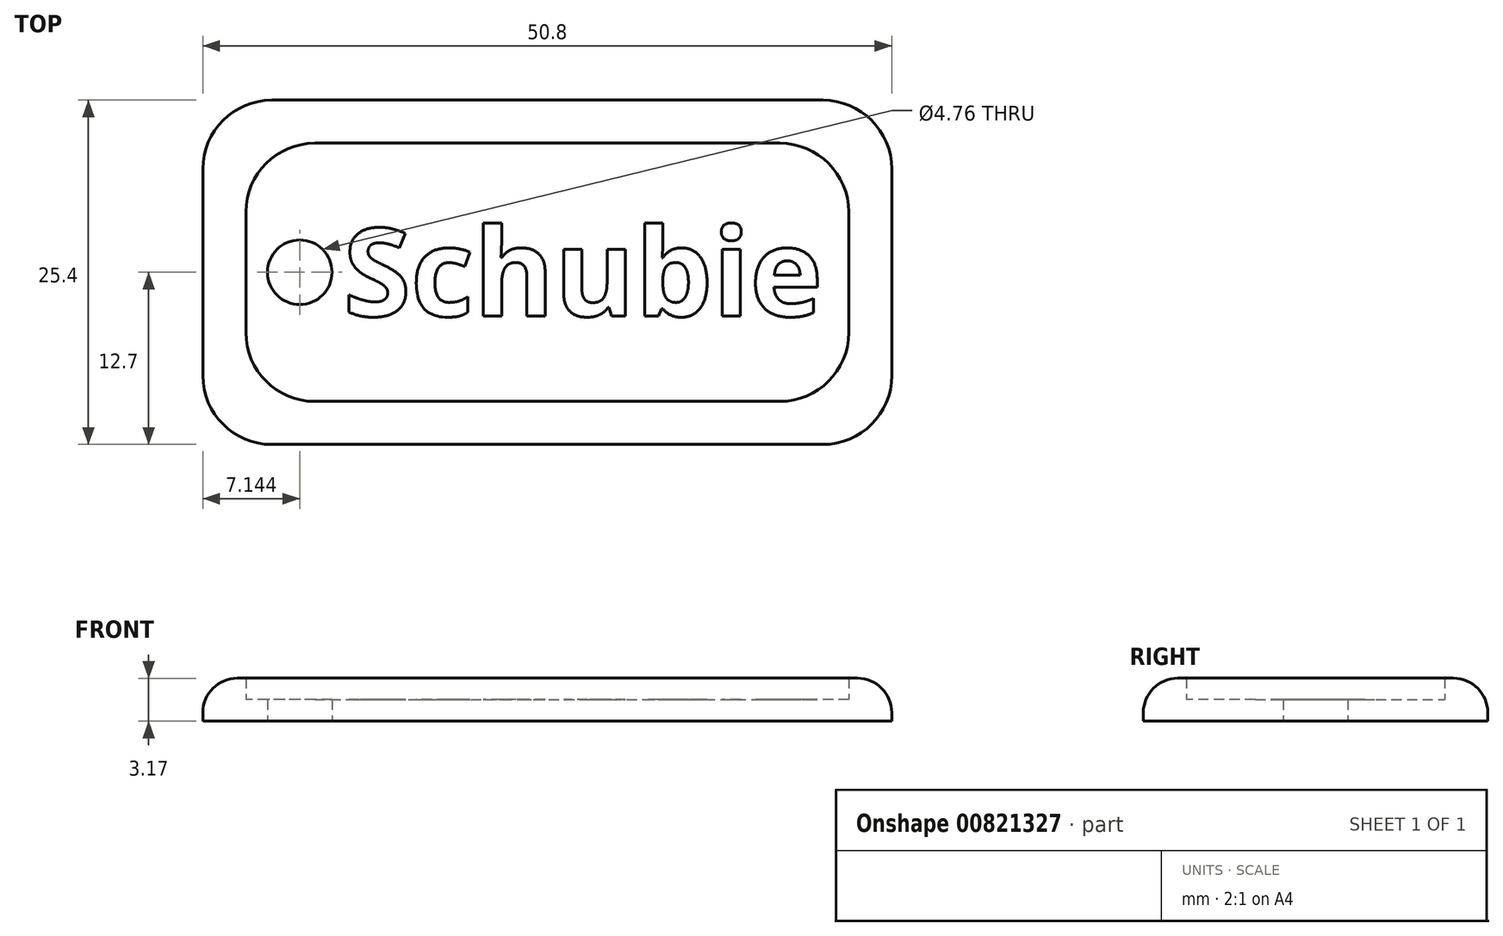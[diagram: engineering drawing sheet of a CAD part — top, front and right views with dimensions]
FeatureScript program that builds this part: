
annotation { "Feature Type Name" : "Feature", "Feature Type Description" : "" }
export const myFeature = defineFeature(function(context is Context, id is Id, definition is map)
    precondition{}
    {
        {
            var Q0;
            Q0=qCreatedBy(makeId("Top.planeOp"),FACE);
            var sketch = newSketch(context, id + "F0", { "sketchPlane" : qUnion([Q0])});
            skLineSegment(sketch, "E0.bottom", {"start": v(0, 0) * mm, "end": v(50.8, 0) * mm});
            skLineSegment(sketch, "E0.top", {"start": v(0, 25.4) * mm, "end": v(50.8, 25.4) * mm});
            skLineSegment(sketch, "E0.left", {"start": v(0, 0) * mm, "end": v(0, 25.4) * mm});
            skLineSegment(sketch, "E0.right", {"start": v(50.8, 0) * mm, "end": v(50.8, 25.4) * mm});
            skCircle(sketch, "E1", {"center": v(7.14, 12.7) * mm, "radius": 2.38 * mm});
            skPoint(sketch, "E1.centerSnap0", {"position": v(0, 12.7) * mm});
            skLineSegment(sketch, "E2.0", {"start": v(3.18, 22.23) * mm, "end": v(47.62, 22.23) * mm});
            skLineSegment(sketch, "E2.1", {"start": v(3.18, 3.18) * mm, "end": v(3.18, 22.22) * mm});
            skLineSegment(sketch, "E2.2", {"start": v(3.18, 3.18) * mm, "end": v(47.62, 3.18) * mm});
            skLineSegment(sketch, "E2.3", {"start": v(47.62, 3.18) * mm, "end": v(47.62, 22.23) * mm});
            skSolve(sketch);
        }
        {
            var Q0;
            Q0=makeQuery(id+"F0.imprint","IMPRINT",FACE,{"disambiguationData":[TD([[makeQuery(id+"F0.imprint","IMPRINT",EDGE,{"derivedFrom":sQuery(id+"F0.wireOp",EDGE,"E1")}),-1.0]])]});
            extrude(context, id + "F1", {"entities" : qUnion([Q0]), "depth" : 1.59 * mm, "offsetDistance" : 25.4 * mm});
        }
        {
            var Q0;
            Q0 = qSketchRegion(id + "F0", true);
            extrude(context, id + "F2", {"entities" : qUnion([Q0]), "operationType" : NewBodyOperationType.ADD, "depth" : 3.17 * mm, "offsetDistance" : 25.4 * mm});
        }
        {
            var Q0;
            Q0=makeQuery(id+"F2.opExtrude","SWEPT_EDGE",EDGE,{"disambiguationData":[OSD([sQuery(id+"F0.wireOp",EDGE,"E0.bottom"),sQuery(id+"F0.wireOp",EDGE,"E0.left")])]});
            var Q1;
            Q1=makeQuery(id+"F2.opExtrude","SWEPT_EDGE",EDGE,{"disambiguationData":[OSD([sQuery(id+"F0.wireOp",EDGE,"E0.bottom"),sQuery(id+"F0.wireOp",EDGE,"E0.right")])]});
            var Q2;
            Q2=makeQuery(id+"F2.opExtrude","SWEPT_EDGE",EDGE,{"disambiguationData":[OSD([sQuery(id+"F0.wireOp",EDGE,"E0.top"),sQuery(id+"F0.wireOp",EDGE,"E0.right")])]});
            var Q3;
            Q3=makeQuery(id+"F2.opExtrude","SWEPT_EDGE",EDGE,{"disambiguationData":[OSD([sQuery(id+"F0.wireOp",EDGE,"E0.top"),sQuery(id+"F0.wireOp",EDGE,"E0.left")])]});
            fillet(context, id + "F3", {"entities" : qUnion([Q0, Q1, Q2, Q3]), "radius" : 5.08 * mm, "tangentPropagation" : true, "allowEdgeOverflow" : false});
        }
        {
            var Q0;
            Q0=makeQuery(id+"F2.opExtrude","SWEPT_EDGE",EDGE,{"disambiguationData":[OSD([sQuery(id+"F0.wireOp",EDGE,"E2.0"),sQuery(id+"F0.wireOp",EDGE,"E2.1")])]});
            var Q1;
            Q1=makeQuery(id+"F2.opExtrude","SWEPT_EDGE",EDGE,{"disambiguationData":[OSD([sQuery(id+"F0.wireOp",EDGE,"E2.1"),sQuery(id+"F0.wireOp",EDGE,"E2.2")])]});
            var Q2;
            Q2=makeQuery(id+"F2.opExtrude","SWEPT_EDGE",EDGE,{"disambiguationData":[OSD([sQuery(id+"F0.wireOp",EDGE,"E2.2"),sQuery(id+"F0.wireOp",EDGE,"E2.3")])]});
            var Q3;
            Q3=makeQuery(id+"F2.opExtrude","SWEPT_EDGE",EDGE,{"disambiguationData":[OSD([sQuery(id+"F0.wireOp",EDGE,"E2.0"),sQuery(id+"F0.wireOp",EDGE,"E2.3")])]});
            fillet(context, id + "F4", {"entities" : qUnion([Q0, Q1, Q2, Q3]), "radius" : 5.08 * mm, "tangentPropagation" : true, "allowEdgeOverflow" : false});
        }
        {
            var Q0;
            Q0=makeQuery(id+"F1.opExtrude","CAP_FACE",FACE,{"disambiguationData":[OSD([sQuery(id+"F0.wireOp",EDGE,"E1"),sQuery(id+"F0.wireOp",EDGE,"E2.0"),sQuery(id+"F0.wireOp",EDGE,"E2.1"),sQuery(id+"F0.wireOp",EDGE,"E2.2"),sQuery(id+"F0.wireOp",EDGE,"E2.3")])],"isStart":false});
            var sketch = newSketch(context, id + "F5", { "sketchPlane" : qUnion([Q0])});
            skText(sketch, "E3", { "text": "Schubie", "fontName": "OpenSans-Bold.ttf"});
            const initialGuessF5  = {"E3": [0.01035, 0.00947, 1, 0, 0.00651]};
            skSetInitialGuess(sketch, initialGuessF5);
            skSolve(sketch);
        }
        {
            var Q0;
            Q0 = qSketchRegion(id + "F5", true);
            extrude(context, id + "F6", {"entities" : qUnion([Q0]), "operationType" : NewBodyOperationType.ADD, "depth" : 1 / 812.8 * mm, "offsetDistance" : 25.4 * mm});
        }
        {
            var Q0;
            Q0=makeQuery(id+"F2.opExtrude","CAP_EDGE",EDGE,{"disambiguationData":[OSD([sQuery(id+"F0.wireOp",EDGE,"E0.bottom")])],"isStart":false});
            fillet(context, id + "F7", {"entities" : qUnion([Q0]), "radius" : 2.54 * mm, "tangentPropagation" : true, "allowEdgeOverflow" : false});
        }
    });
